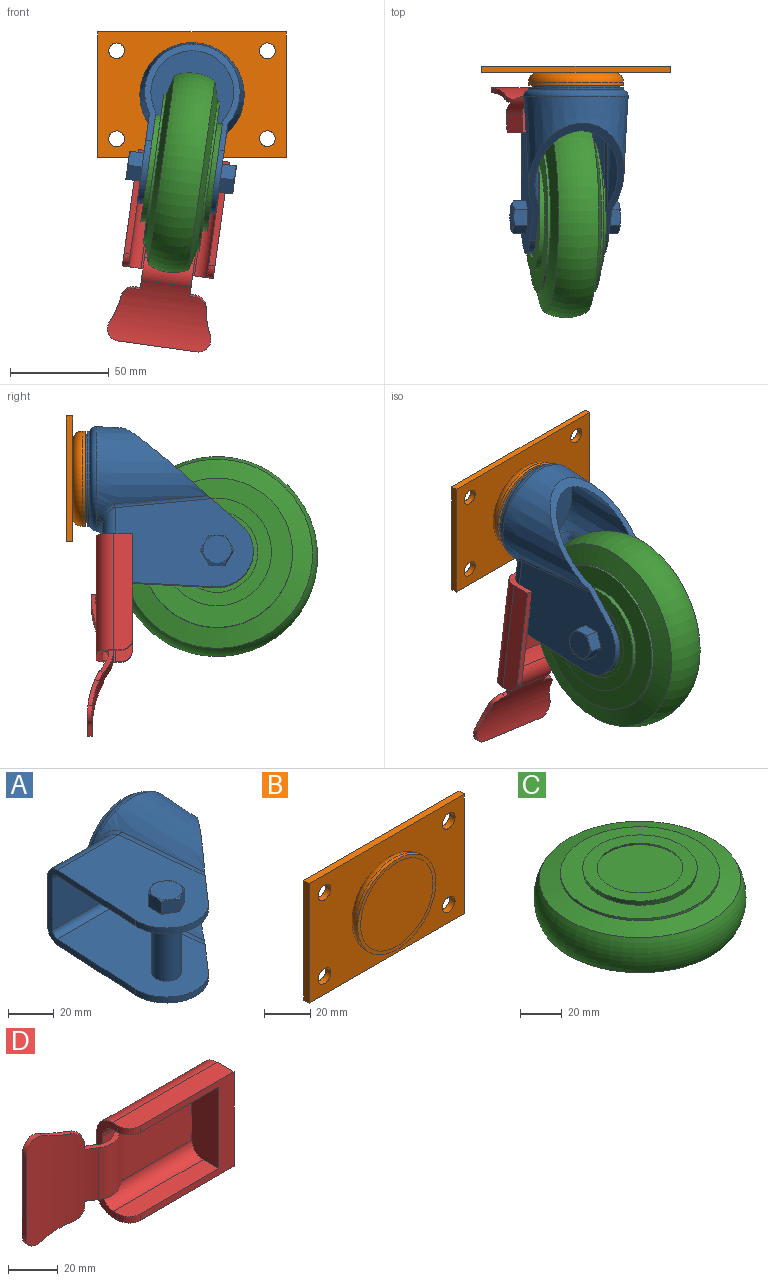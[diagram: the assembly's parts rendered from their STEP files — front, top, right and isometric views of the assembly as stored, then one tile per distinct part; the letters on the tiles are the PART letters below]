
ASSEMBLY  parts=4 mates=3
PART A: 64 faces, bbox 87.2x107.6x57.8 mm
  f0: plane 48.01x48.01mm, normal (0,-1,0), area 119.5mm2, adj f3,f14
  f1: cylinder r=22.23mm len=44.45mm, axis (0,1,0), area 159.6mm2, adj f2,f63
  f2: plane 48.01x48.01mm, normal (0,1,0), area 258.2mm2, adj f1,f3
  f3: cylinder r=24mm len=48.01mm, axis (0,1,0), area 195.4mm2, adj f0,f2
  f4: plane 69.86x45.07mm, normal (0,0,-1), area 2508.5mm2, adj f10,f12,f20,f22,f23,f50,f51,f52
  f5: plane 69.86x45.07mm, normal (0,0,1), area 2508.5mm2, adj f9,f13,f21,f22,f23,f37,f38,f39
  f6: plane 69.86x45.07mm, normal (0,0,1), area 2558.6mm2, adj f20,f22,f23,f31,f33,f36
  f7: plane 69.86x45.07mm, normal (0,0,-1), area 2558.6mm2, adj f21,f22,f23,f30,f34,f36
  f8: plane 28.73x27.31mm, normal (0,1,0), area 722.8mm2, adj f9,f10,f17,f22
  f9: cylinder r=6.35mm len=37.74mm, axis (1,0,0), area 331.5mm2, adj f5,f8,f18,f19,f22
  f10: cylinder r=6.35mm len=37.74mm, axis (-1,0,0), area 331.5mm2, adj f4,f8,f15,f16,f22
  f11: cone r=26.54mm half-angle=3deg, axis (0,1,0), area 3567.4mm2, adj f12,f13,f14,f15,f19,f23
  f12: bspline ~94.12x10.11mm, area 89.2mm2, adj f4,f11,f15,f23
  f13: bspline ~75.77x8.62mm, area 89.2mm2, adj f5,f11,f19,f23
  f14: torus R=23.2mm, axis (0,-1,0), area 813.2mm2, adj f0,f11,f16,f17,f18
  f15: bspline ~10.9x9.63mm, area 39.4mm2, adj f10,f11,f12,f16
  f16: bspline ~6.07x5.43mm, area 10.9mm2, adj f10,f14,f15,f17
  f17: torus R=29.55mm, axis (0,-1,0), area 131.9mm2, adj f8,f14,f16,f18
  f18: bspline ~6.07x5.43mm, area 10.9mm2, adj f9,f14,f17,f19
  f19: bspline ~10.93x9.75mm, area 39.4mm2, adj f9,f11,f13,f18
  f20: cylinder r=18.26mm len=32.04mm, axis (0,0,-1), area 143.7mm2, adj f4,f6,f22,f23
  f21: cylinder r=18.26mm len=32.04mm, axis (0,0,-1), area 143.7mm2, adj f5,f7,f22,f23
  f22: plane 57.13x40.14mm, normal (-1,0.05,0), area 456.4mm2, adj f4,f5,f6,f7,f8,f9,f10,f20
  f23: plane 59.48x51.63mm, normal (0.76,-0.66,0), area 628.3mm2, adj f4,f5,f6,f7,f11,f12,f13,f20
  f24: torus R=29.55mm, axis (0,-1,0), area 244.4mm2, adj f25,f26,f27,f35
  f25: bspline ~8.95x6.93mm, area 15.4mm2, adj f24,f27,f29,f34
  f26: bspline ~8.95x6.93mm, area 15.4mm2, adj f24,f27,f28,f33
  f27: plane 46.41x46.41mm, normal (0,-1,0), area 1690.5mm2, adj f24,f25,f26,f32
  f28: bspline ~11.54x9.83mm, area 62.5mm2, adj f26,f31,f32,f33
  f29: bspline ~11.66x10.93mm, area 62.5mm2, adj f25,f30,f32,f34
  f30: bspline ~75.94x10.07mm, area 176mm2, adj f7,f23,f29,f32
  f31: bspline ~94.28x11.56mm, area 176mm2, adj f6,f23,f28,f32
  f32: cone r=23.37mm half-angle=3deg, axis (0,1,0), area 3289.1mm2, adj f23,f27,f28,f29,f30,f31
  f33: cylinder r=3.17mm len=37.74mm, axis (-1,0,0), area 166.2mm2, adj f6,f22,f26,f28,f35
  f34: cylinder r=3.17mm len=37.74mm, axis (1,0,0), area 166.2mm2, adj f7,f22,f25,f29,f35
  f35: plane 28.89x27.31mm, normal (0,-1,0), area 727.4mm2, adj f22,f24,f33,f34
  f36: cylinder r=6.35mm len=33.66mm, axis (0,0,-1), area 1342.8mm2, adj f6,f7
  f37: plane 7.92x7.82mm, normal (-0.5,-0.87,0), area 57.9mm2, adj f5,f38,f42,f44,f45
  f38: plane 7.92x7.82mm, normal (0.5,-0.87,0), area 57.9mm2, adj f5,f37,f39,f43,f44
  f39: plane 8.94x7.92mm, normal (1,0,0), area 57.9mm2, adj f5,f38,f40,f43,f48
  f40: plane 7.92x7.82mm, normal (0.5,0.87,0), area 57.9mm2, adj f5,f39,f41,f47,f48
  f41: plane 7.92x7.82mm, normal (-0.5,0.87,0), area 57.9mm2, adj f5,f40,f42,f46,f47
  f42: plane 8.94x7.92mm, normal (-1,0,0), area 57.9mm2, adj f5,f37,f41,f45,f46
  f43: cone r=7.14mm half-angle=60deg, axis (0,0,-1), area 5mm2, adj f38,f39,f49
  f44: cone r=7.14mm half-angle=60deg, axis (0,0,-1), area 5mm2, adj f37,f38,f49
  f45: cone r=7.14mm half-angle=60deg, axis (0,0,-1), area 5mm2, adj f37,f42,f49
  f46: cone r=7.14mm half-angle=60deg, axis (0,0,-1), area 5mm2, adj f41,f42,f49
  f47: cone r=7.14mm half-angle=60deg, axis (0,0,-1), area 5mm2, adj f40,f41,f49
  f48: cone r=7.14mm half-angle=60deg, axis (0,0,-1), area 5mm2, adj f39,f40,f49
  f49: plane 14.29x14.29mm, normal (0,0,1), area 160.3mm2, adj f43,f44,f45,f46,f47,f48
  f50: plane 7.92x7.82mm, normal (-0.5,-0.87,0), area 57.9mm2, adj f4,f51,f55,f57,f58
  f51: plane 7.92x7.82mm, normal (0.5,-0.87,0), area 57.9mm2, adj f4,f50,f52,f56,f57
  f52: plane 8.94x7.92mm, normal (1,0,0), area 57.9mm2, adj f4,f51,f53,f56,f61
  f53: plane 7.92x7.82mm, normal (0.5,0.87,0), area 57.9mm2, adj f4,f52,f54,f60,f61
  f54: plane 7.92x7.82mm, normal (-0.5,0.87,0), area 57.9mm2, adj f4,f53,f55,f59,f60
  f55: plane 8.94x7.92mm, normal (-1,0,0), area 57.9mm2, adj f4,f50,f54,f58,f59
  f56: cone r=7.14mm half-angle=60deg, axis (0,0,1), area 5mm2, adj f51,f52,f62
  f57: cone r=7.14mm half-angle=60deg, axis (0,0,1), area 5mm2, adj f50,f51,f62
  f58: cone r=7.14mm half-angle=60deg, axis (0,0,1), area 5mm2, adj f50,f55,f62
  f59: cone r=7.14mm half-angle=60deg, axis (0,0,1), area 5mm2, adj f54,f55,f62
  f60: cone r=7.14mm half-angle=60deg, axis (0,0,1), area 5mm2, adj f53,f54,f62
  f61: cone r=7.14mm half-angle=60deg, axis (0,0,1), area 5mm2, adj f52,f53,f62
  f62: plane 14.29x14.29mm, normal (0,0,-1), area 160.3mm2, adj f56,f57,f58,f59,f60,f61
  f63: plane 44.45x44.45mm, normal (0,1,0), area 1551.8mm2, adj f1
PART B: 14 faces, bbox 95.3x9.5x63.5 mm
  f0: plane 95.25x63.5mm, normal (0,1,0), area 5850.4mm2, adj f1,f2,f3,f4,f5,f6,f7,f8
  f1: cylinder r=3.97mm len=7.94mm, axis (0,1,0), area 79.2mm2, adj f0,f9
  f2: cylinder r=3.97mm len=7.94mm, axis (0,1,0), area 79.2mm2, adj f0,f9
  f3: cylinder r=3.97mm len=7.94mm, axis (0,1,0), area 79.2mm2, adj f0,f9
  f4: cylinder r=3.97mm len=7.94mm, axis (0,1,0), area 79.2mm2, adj f0,f9
  f5: plane 95.25x3.18mm, normal (0,0,1), area 302.4mm2, adj f0,f6,f8,f9
  f6: plane 63.5x3.18mm, normal (1,0,0), area 201.6mm2, adj f0,f5,f7,f9
  f7: plane 95.25x3.18mm, normal (0,0,-1), area 302.4mm2, adj f0,f6,f8,f9
  f8: plane 63.5x3.18mm, normal (-1,0,0), area 201.6mm2, adj f0,f5,f7,f9
  f9: plane 95.25x63.5mm, normal (0,-1,0), area 4687.4mm2, adj f1,f2,f3,f4,f5,f6,f7,f8
  f10: torus R=19.24mm, axis (0,1,0), area 1046.9mm2, adj f9,f11
  f11: cylinder r=24mm len=48.01mm, axis (0,1,0), area 229.8mm2, adj f10,f12
  f12: plane 48.01x48.01mm, normal (0,-1,0), area 258.2mm2, adj f11,f13
  f13: plane 44.45x44.45mm, normal (0,-1,0), area 1551.8mm2, adj f12
PART C: 15 faces, bbox 110x110x34 mm
  f0: plane 42.86x42.86mm, normal (0,0,1), area 1442.9mm2, adj f1
  f1: cone r=20.59mm half-angle=30deg, axis (0,0,-1), area 222.6mm2, adj f0,f2
  f2: plane 54.94x54.94mm, normal (0,0,1), area 1038.9mm2, adj f1,f3
  f3: cone r=26.99mm half-angle=10deg, axis (0,0,1), area 474.3mm2, adj f2,f4
  f4: plane 76.2x76.2mm, normal (0,0,1), area 2272.3mm2, adj f3,f5
  f5: cylinder r=38.1mm len=76.2mm, axis (0,0,-1), area 304mm2, adj f4,f6
  f6: cone r=48.26mm half-angle=75deg, axis (0,0,-1), area 2853.7mm2, adj f5,f7
  f7: torus R=28.67mm, axis (0,0,-1), area 6720.8mm2, adj f6,f8
  f8: cone r=38.1mm half-angle=75deg, axis (0,0,1), area 2853.7mm2, adj f7,f9
  f9: cylinder r=38.1mm len=76.2mm, axis (0,0,-1), area 304mm2, adj f8,f10
  f10: plane 76.2x76.2mm, normal (0,0,-1), area 2272.3mm2, adj f9,f11
  f11: cone r=27.47mm half-angle=10deg, axis (0,0,-1), area 474.3mm2, adj f10,f12
  f12: plane 54.94x54.94mm, normal (0,0,-1), area 1038.9mm2, adj f11,f13
  f13: cone r=21.43mm half-angle=30deg, axis (0,0,1), area 222.6mm2, adj f12,f14
  f14: plane 42.86x42.86mm, normal (0,0,-1), area 1442.9mm2, adj f13
PART D: 38 faces, bbox 97.3x34.6x52.7 mm
  f0: plane 22.91x6.84mm, normal (0,0,1), area 50.5mm2, adj f13,f18,f19,f20,f21,f22,f23,f30
  f1: plane 22.91x6.84mm, normal (0,0,-1), area 50.5mm2, adj f13,f18,f19,f20,f21,f22,f23,f29
  f2: cylinder r=6.35mm len=6.35mm, axis (0,0,1), area 31.7mm2, adj f4,f6,f9,f15
  f3: plane 46.36x18.42mm, normal (1,0,0), area 819.7mm2, adj f4,f7,f8,f9,f10,f11
  f4: plane 53x46.36mm, normal (0,-1,0), area 678.7mm2, adj f2,f3,f5,f8,f9,f15,f16,f17
  f5: cylinder r=6.35mm len=6.35mm, axis (0,0,1), area 31.7mm2, adj f4,f6,f8,f16
  f6: plane 46.36x12.07mm, normal (-1,0,0), area 187mm2, adj f2,f5,f7,f8,f9,f10,f11,f12
  f7: plane 59.35x28.58mm, normal (0,1,0), area 1447.3mm2, adj f3,f6,f10,f11,f24,f26,f27,f28
  f8: plane 59.35x9.53mm, normal (0,0,-1), area 556.7mm2, adj f3,f4,f5,f6,f11
  f9: plane 59.35x9.53mm, normal (0,0,1), area 556.7mm2, adj f2,f3,f4,f6,f10
  f10: cylinder r=8.89mm len=59.35mm, axis (-1,0,0), area 828.8mm2, adj f3,f6,f7,f9
  f11: cylinder r=8.89mm len=59.35mm, axis (-1,0,0), area 828.8mm2, adj f3,f6,f7,f8
  f12: cylinder r=6.35mm len=50.8mm, axis (-1,0,0), area 506.7mm2, adj f6,f13,f16,f17
  f13: plane 50.8x27.31mm, normal (0,-1,0), area 1260.2mm2, adj f0,f1,f6,f12,f14,f17,f22,f23
  f14: cylinder r=6.35mm len=50.8mm, axis (-1,0,0), area 506.7mm2, adj f6,f13,f15,f17
  f15: plane 50.8x8.89mm, normal (0,0,-1), area 443mm2, adj f2,f4,f6,f14,f17
  f16: plane 50.8x8.89mm, normal (0,0,1), area 443mm2, adj f4,f5,f6,f12,f17
  f17: plane 40.01x15.24mm, normal (-1,0,0), area 592.4mm2, adj f4,f12,f13,f14,f15,f16
  f18: cylinder r=7.94mm len=25.4mm, axis (0,0,-1), area 246.8mm2, adj f0,f1,f19,f22
  f19: cylinder r=50.8mm len=52.71mm, axis (0,0,-1), area 1531.1mm2, adj f0,f1,f18,f29,f30,f31,f32,f33
  f20: cylinder r=48.51mm len=52.71mm, axis (0,0,-1), area 1473.9mm2, adj f0,f1,f21,f29,f30,f31,f32,f33
  f21: cylinder r=10.22mm len=25.4mm, axis (0,0,-1), area 317.8mm2, adj f0,f1,f20,f23
  f22: cylinder r=41.96mm len=25.4mm, axis (0,0,-1), area 83.1mm2, adj f0,f1,f13,f18
  f23: cylinder r=39.68mm len=25.4mm, axis (0,0,-1), area 188.3mm2, adj f0,f1,f13,f21
  f24: cylinder r=39.68mm len=25.4mm, axis (0,0,-1), area 147.4mm2, adj f7,f25,f27,f28
  f25: plane 25.4x2.29mm, normal (1,-0.03,0), area 58.1mm2, adj f24,f26,f27,f28
  f26: cylinder r=41.96mm len=25.4mm, axis (0,0,-1), area 405.1mm2, adj f7,f25,f27,f28
  f27: plane 15.65x2.56mm, normal (0,0,1), area 26.6mm2, adj f7,f24,f25,f26
  f28: plane 15.65x2.56mm, normal (0,0,-1), area 26.6mm2, adj f7,f24,f25,f26
  f29: plane 2.67x2mm, normal (0.88,-0.48,0), area 5.9mm2, adj f1,f19,f20,f36
  f30: plane 2.67x2mm, normal (0.88,-0.48,0), area 5.9mm2, adj f0,f19,f20,f37
  f31: plane 40.01x2.29mm, normal (-1,0,0), area 91.7mm2, adj f19,f20,f32,f35
  f32: cylinder r=6.35mm len=9.13mm, axis (0,1,0), area 29.5mm2, adj f19,f20,f31,f33
  f33: cylinder r=44mm len=14.11mm, axis (0,1,0), area 32.9mm2, adj f19,f20,f32,f36
  f34: cylinder r=44mm len=14.11mm, axis (0,1,0), area 32.9mm2, adj f19,f20,f35,f37
  f35: cylinder r=6.35mm len=9.13mm, axis (0,1,0), area 29.5mm2, adj f19,f20,f31,f34
  f36: bspline ~34.63x21.01mm, area 21.1mm2, adj f19,f20,f29,f33
  f37: bspline ~34.63x21.01mm, area 21.1mm2, adj f19,f20,f30,f34
PLACE A rot(axis=(0,-1,0),82.1deg) t=(0,0,0)mm
PLACE B at identity fixed
PLACE C rot(axis=(0,-1,0),82.1deg) t=(0.19,0,-0.03)mm
PLACE D rot(axis=(0,-1,0),82.1deg) t=(0.19,0,-0.03)mm
MATE planar D.f13 <-> A.f8  axis (0,-1,0) through (-8.54,-18.25,-62.94)mm
MATE revolute A.f1 <-> B.f10  axis (0,1,0) through (0,-9.46,0)mm
MATE revolute A.f20 <-> C.f1  axis (0.99,0,-0.14) through (-22.12,-76.2,-37)mm
